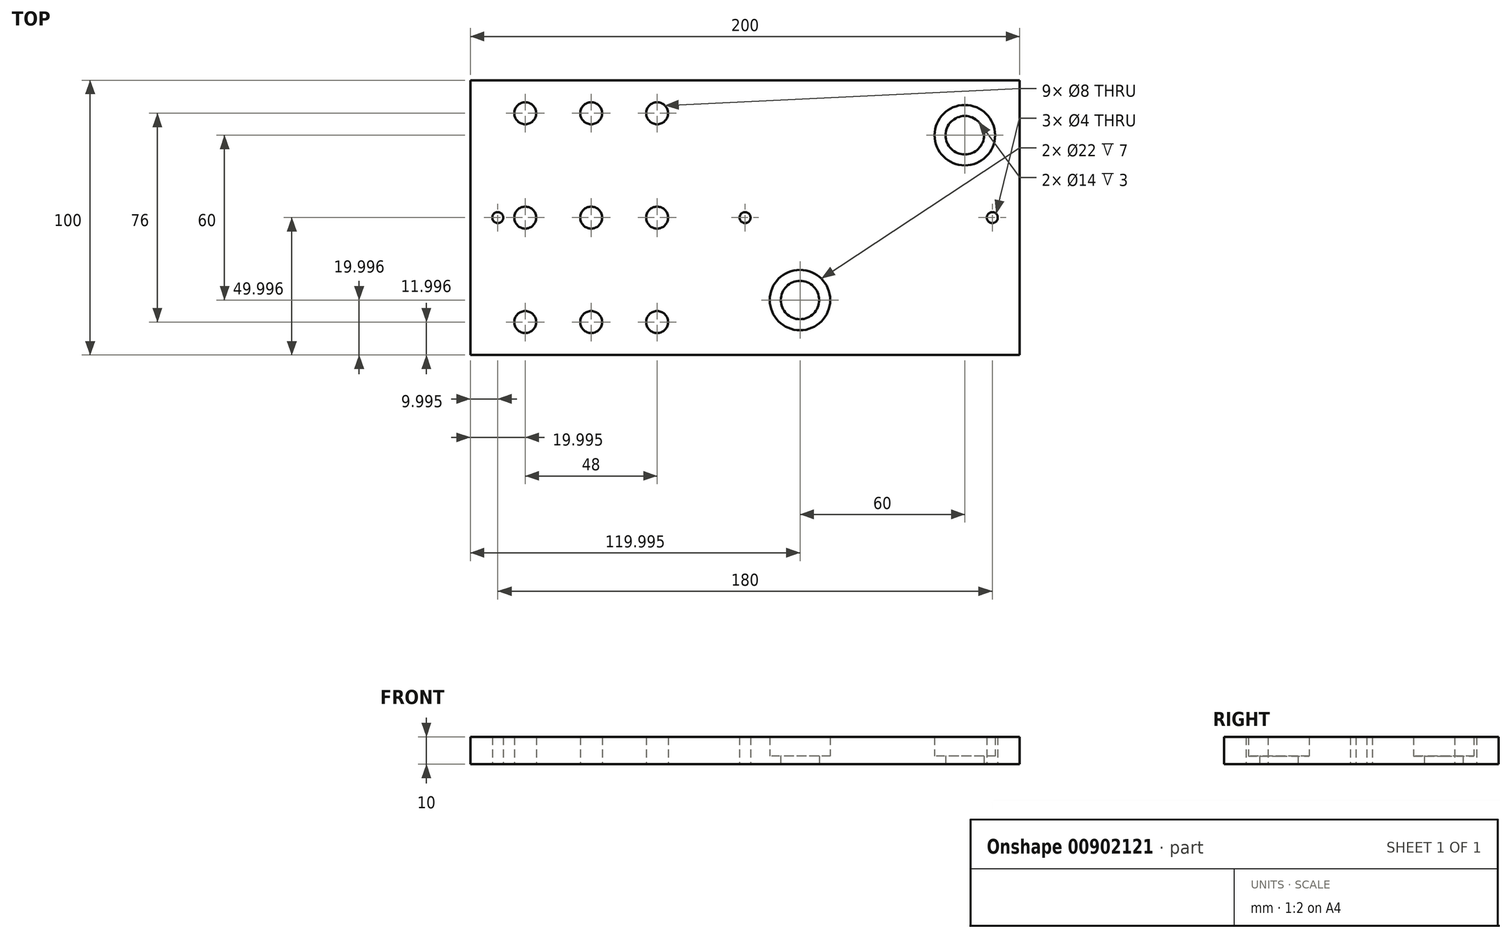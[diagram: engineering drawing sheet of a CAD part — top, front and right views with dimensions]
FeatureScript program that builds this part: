
annotation { "Feature Type Name" : "Feature", "Feature Type Description" : "" }
export const myFeature = defineFeature(function(context is Context, id is Id, definition is map)
    precondition{}
    {
        {
            var Q0;
            Q0=qCreatedBy(makeId("Top.planeOp"),FACE);
            var sketch = newSketch(context, id + "F0", { "sketchPlane" : qUnion([Q0])});
            skLineSegment(sketch, "E0.bottom", {"start": v(-136.01, 62.84) * mm, "end": v(63.99, 62.84) * mm});
            skLineSegment(sketch, "E0.top", {"start": v(-136.01, -37.16) * mm, "end": v(63.99, -37.16) * mm});
            skLineSegment(sketch, "E0.left", {"start": v(-136.01, 62.84) * mm, "end": v(-136.01, -37.16) * mm});
            skLineSegment(sketch, "E0.right", {"start": v(63.99, 62.84) * mm, "end": v(63.99, -37.16) * mm});
            skCircle(sketch, "E1", {"center": v(-116.01, 50.84) * mm, "radius": 4 * mm});
            skCircle(sketch, "E2.MirrorC", {"center": v(-116.01, -25.16) * mm, "radius": 4 * mm});
            skCircle(sketch, "E3.MirrorC", {"center": v(-68.01, 50.84) * mm, "radius": 4 * mm});
            skCircle(sketch, "E4.MirrorC", {"center": v(-68.01, -25.16) * mm, "radius": 4 * mm});
            skCircle(sketch, "E5", {"center": v(-126.01, 12.84) * mm, "radius": 2 * mm});
            skCircle(sketch, "E6", {"center": v(-36.01, 12.84) * mm, "radius": 2 * mm});
            skCircle(sketch, "E7", {"center": v(53.99, 12.84) * mm, "radius": 2 * mm});
            skCircle(sketch, "E8", {"center": v(-16.01, -17.16) * mm, "radius": 7 * mm});
            skCircle(sketch, "E9", {"center": v(43.99, 42.84) * mm, "radius": 7 * mm});
            skCircle(sketch, "E10", {"center": v(-16.01, -17.16) * mm, "radius": 11 * mm});
            skCircle(sketch, "E11", {"center": v(43.99, 42.84) * mm, "radius": 11 * mm});
            skCircle(sketch, "E12", {"center": v(-92.01, 50.84) * mm, "radius": 4 * mm});
            skCircle(sketch, "E13", {"center": v(-92.01, -25.16) * mm, "radius": 4 * mm});
            skCircle(sketch, "E14", {"center": v(-116.01, 12.84) * mm, "radius": 4 * mm});
            skCircle(sketch, "E15", {"center": v(-92.01, 12.84) * mm, "radius": 4 * mm});
            skCircle(sketch, "E16", {"center": v(-68.01, 12.84) * mm, "radius": 4 * mm});
            skSolve(sketch);
        }
        {
            var Q0;
            Q0=makeQuery(id+"F0.imprint","IMPRINT",FACE,{"disambiguationData":[TD([[makeQuery(id+"F0.imprint","IMPRINT",EDGE,{"derivedFrom":sQuery(id+"F0.wireOp",EDGE,"E0.bottom")}),-1.0]])]});
            extrude(context, id + "F1", {"entities" : qUnion([Q0]), "depth" : 10 * mm, "offsetDistance" : 25 * mm});
        }
        {
            var Q0;
            Q0=makeQuery(id+"F0.imprint","IMPRINT",FACE,{"disambiguationData":[TD([[makeQuery(id+"F0.imprint","IMPRINT",EDGE,{"derivedFrom":sQuery(id+"F0.wireOp",EDGE,"E8")}),-1.0]])]});
            var Q1;
            Q1=makeQuery(id+"F0.imprint","IMPRINT",FACE,{"disambiguationData":[TD([[makeQuery(id+"F0.imprint","IMPRINT",EDGE,{"derivedFrom":sQuery(id+"F0.wireOp",EDGE,"E9")}),-1.0]])]});
            extrude(context, id + "F2", {"entities" : qUnion([Q0, Q1]), "operationType" : NewBodyOperationType.ADD, "depth" : 3 * mm, "offsetDistance" : 25 * mm});
        }
    });
